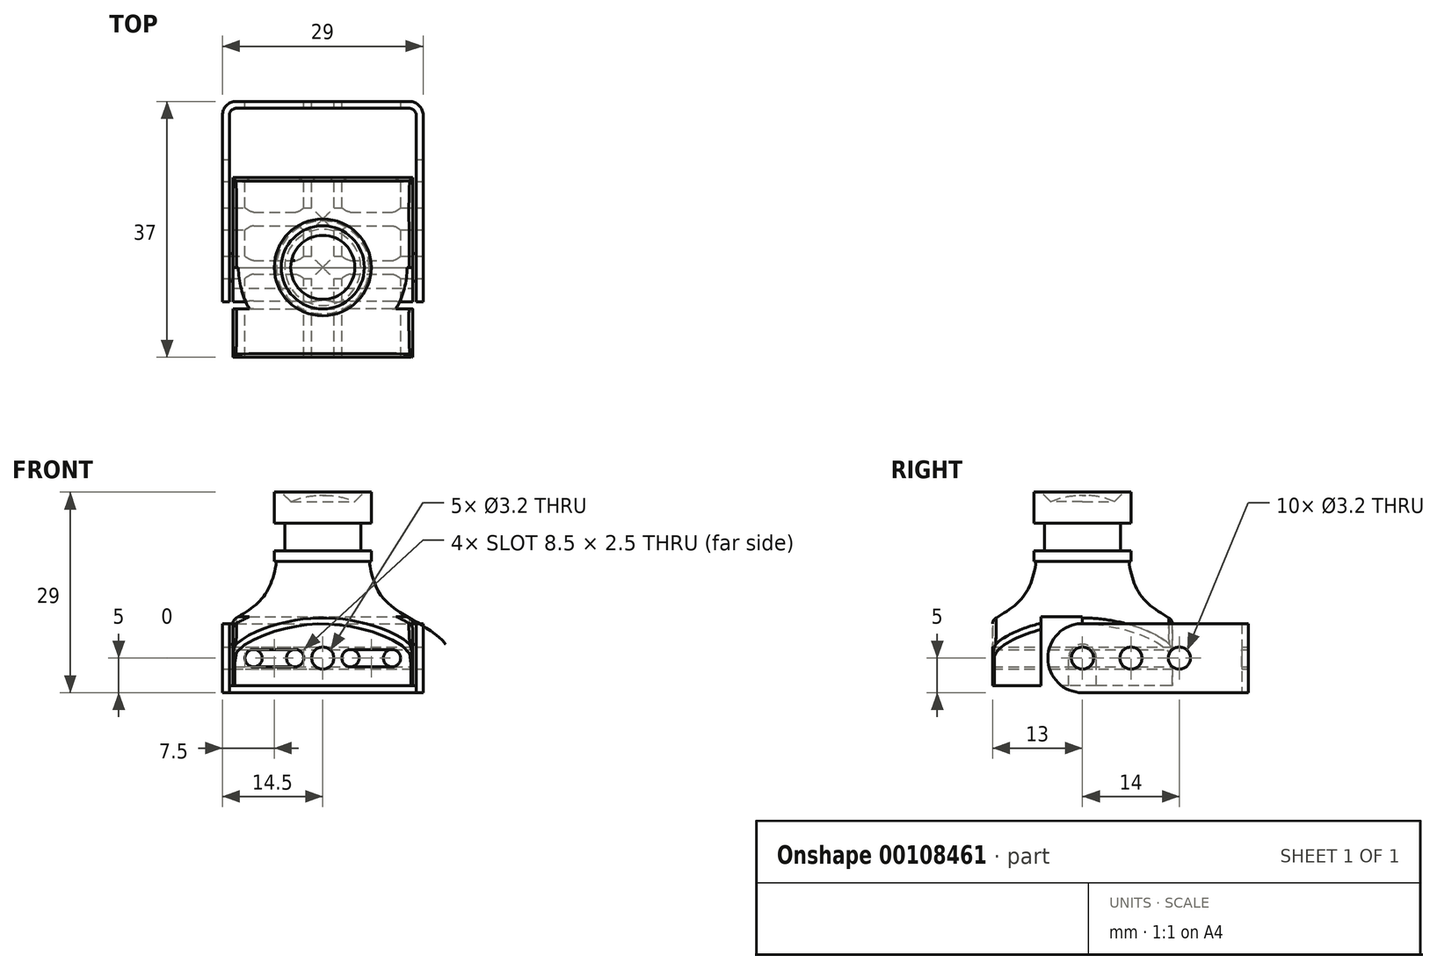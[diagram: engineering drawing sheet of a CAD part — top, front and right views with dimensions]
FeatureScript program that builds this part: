
annotation { "Feature Type Name" : "Feature", "Feature Type Description" : "" }
export const myFeature = defineFeature(function(context is Context, id is Id, definition is map)
    precondition{}
    {
        {
            var Q0;
            Q0=qCreatedBy(makeId("Front.planeOp"),FACE);
            var sketch = newSketch(context, id + "F0", { "sketchPlane" : qUnion([Q0])});
            skLineSegment(sketch, "E0", {"start": v(0, 0) * mm, "end": v(0, 27.5) * mm});
            skLineSegment(sketch, "E1", {"start": v(7, 28) * mm, "end": v(7, 23.5) * mm});
            skLineSegment(sketch, "E2", {"start": v(7, 23.5) * mm, "end": v(5.5, 23.5) * mm});
            skLineSegment(sketch, "E3", {"start": v(5.5, 23.5) * mm, "end": v(5.5, 19.5) * mm});
            skLineSegment(sketch, "E4", {"start": v(5.5, 19.5) * mm, "end": v(7, 19.5) * mm});
            skLineSegment(sketch, "E5", {"start": v(7, 19.5) * mm, "end": v(7, 18) * mm});
            skLineSegment(sketch, "E6", {"start": v(7, 18) * mm, "end": v(6.7, 18) * mm});
            skFitSpline(sketch, "E7", {"points": [v(6.7, 18) * mm, v(8.96, 12.41) * mm, v(13.5, 9.25) * mm, v(17.33, 6.49) * mm, v(18.5, 4) * mm], "startDerivative": vector(3.38, -24.57) * mm, "endDerivative": vector(0, -14.16) * mm});
            skLineSegment(sketch, "E8", {"start": v(7, 28) * mm, "end": v(6, 28) * mm});
            skLineSegment(sketch, "E9", {"start": v(6, 28) * mm, "end": v(4.63, 26.63) * mm});
            skFitSpline(sketch, "E10", {"points": [v(0, 27.5) * mm, v(4.63, 26.63) * mm], "startDerivative": vector(5.21, 0.16) * mm, "endDerivative": vector(4.71, -2.1) * mm});
            skLineSegment(sketch, "E11", {"start": v(18.5, 4) * mm, "end": v(18.5, 0) * mm});
            skLineSegment(sketch, "E12", {"start": v(18.5, 0) * mm, "end": v(0, 0) * mm});
            skSolve(sketch);
        }
        {
            var Q0;
            Q0 = qSketchRegion(id + "F0", true);
            var Q1;
            Q1=sQuery(id+"F0.wireOp",EDGE,"E0");
            revolve(context, id + "F1", {"entities" : qUnion([Q0]), "axis" : qUnion([Q1]), "revolveType" : RevolveType.FULL});
        }
        {
            var Q0;
            Q0=qCreatedBy(makeId("Right.planeOp"),FACE);
            var sketch = newSketch(context, id + "F2", { "sketchPlane" : qUnion([Q0])});
            skLineSegment(sketch, "E13", {"start": v(-13, 0) * mm, "end": v(-13, 12) * mm});
            skLineSegment(sketch, "E14", {"start": v(-13, 12) * mm, "end": v(-20, 12) * mm});
            skLineSegment(sketch, "E15", {"start": v(-20, 12) * mm, "end": v(-20, -2) * mm});
            skLineSegment(sketch, "E16", {"start": v(-20, -2) * mm, "end": v(0, -2) * mm});
            skLineSegment(sketch, "E17", {"start": v(-13, 0) * mm, "end": v(0, 0) * mm});
            skLineSegment(sketch, "E18.MirrorCS", {"start": v(13, 0) * mm, "end": v(13, 12) * mm});
            skLineSegment(sketch, "E19.MirrorCS", {"start": v(20, 12) * mm, "end": v(20, -2) * mm});
            skLineSegment(sketch, "E20.MirrorCS", {"start": v(13, 0) * mm, "end": v(0, 0) * mm});
            skLineSegment(sketch, "E21.MirrorCS", {"start": v(20, -2) * mm, "end": v(0, -2) * mm});
            skLineSegment(sketch, "E22.MirrorCS", {"start": v(13, 12) * mm, "end": v(20, 12) * mm});
            skSolve(sketch);
        }
        {
            var Q0;
            Q0 = qSketchRegion(id + "F2", true);
            extrude(context, id + "F3", {"entities" : qUnion([Q0]), "operationType" : NewBodyOperationType.REMOVE, "endBound" : BoundingType.THROUGH_ALL, "oppositeDirection" : true, "depth" : 25 * mm, "hasSecondDirection" : true, "secondDirectionBound" : SecondDirectionBoundingType.THROUGH_ALL, "secondDirectionOppositeDirection" : false, "secondDirectionDepth" : 25 * mm});
        }
        {
            var Q0;
            Q0=qCreatedBy(makeId("Front.planeOp"),FACE);
            var sketch = newSketch(context, id + "F4", { "sketchPlane" : qUnion([Q0])});
            skLineSegment(sketch, "E23", {"start": v(-13, 0) * mm, "end": v(-13, 12) * mm});
            skLineSegment(sketch, "E24", {"start": v(-13, 12) * mm, "end": v(-20, 12) * mm});
            skLineSegment(sketch, "E25", {"start": v(-20, 12) * mm, "end": v(-20, -2) * mm});
            skLineSegment(sketch, "E26", {"start": v(-20, -2) * mm, "end": v(0, -2) * mm});
            skLineSegment(sketch, "E27", {"start": v(-13, 0) * mm, "end": v(0, 0) * mm});
            skLineSegment(sketch, "E28.MirrorCS", {"start": v(13, 0) * mm, "end": v(13, 12) * mm});
            skLineSegment(sketch, "E29.MirrorCS", {"start": v(13, 12) * mm, "end": v(20, 12) * mm});
            skLineSegment(sketch, "E30.MirrorCS", {"start": v(20, -2) * mm, "end": v(0, -2) * mm});
            skLineSegment(sketch, "E31.MirrorCS", {"start": v(20, 12) * mm, "end": v(20, -2) * mm});
            skLineSegment(sketch, "E32.MirrorCS", {"start": v(13, 0) * mm, "end": v(0, 0) * mm});
            skSolve(sketch);
        }
        {
            var Q0;
            Q0 = qSketchRegion(id + "F4", true);
            extrude(context, id + "F5", {"entities" : qUnion([Q0]), "operationType" : NewBodyOperationType.REMOVE, "endBound" : BoundingType.THROUGH_ALL, "oppositeDirection" : true, "depth" : 25 * mm, "hasSecondDirection" : true, "secondDirectionBound" : SecondDirectionBoundingType.THROUGH_ALL, "secondDirectionOppositeDirection" : false, "secondDirectionDepth" : 25 * mm});
        }
        {
            var Q0;
            Q0=makeQuery(id+"F3.boolean.opBoolean","INTERSECT",EDGE,{"derivedFrom":[makeQuery(id+"F1.opRevolve","SWEPT_FACE",FACE,{"disambiguationData":[OSD([sQuery(id+"F0.wireOp",EDGE,"E7")])]}),makeQuery(id+"F3.opExtrude","SWEPT_FACE",FACE,{"disambiguationData":[OSD([sQuery(id+"F2.wireOp",EDGE,"E13")])]})]});
            var Q1;
            Q1=makeQuery(id+"F5.boolean.opBoolean","INTERSECT",EDGE,{"derivedFrom":[makeQuery(id+"F1.opRevolve","SWEPT_FACE",FACE,{"disambiguationData":[OSD([sQuery(id+"F0.wireOp",EDGE,"E7")])]}),makeQuery(id+"F5.opExtrude","SWEPT_FACE",FACE,{"disambiguationData":[OSD([sQuery(id+"F4.wireOp",EDGE,"E23")])]})]});
            var Q2;
            Q2=makeQuery(id+"F3.boolean.opBoolean","INTERSECT",EDGE,{"derivedFrom":[makeQuery(id+"F1.opRevolve","SWEPT_FACE",FACE,{"disambiguationData":[OSD([sQuery(id+"F0.wireOp",EDGE,"E7")])]}),makeQuery(id+"F3.opExtrude","SWEPT_FACE",FACE,{"disambiguationData":[OSD([sQuery(id+"F2.wireOp",EDGE,"E18.MirrorCS")])]})]});
            var Q3;
            Q3=makeQuery(id+"F5.boolean.opBoolean","INTERSECT",EDGE,{"derivedFrom":[makeQuery(id+"F1.opRevolve","SWEPT_FACE",FACE,{"disambiguationData":[OSD([sQuery(id+"F0.wireOp",EDGE,"E7")])]}),makeQuery(id+"F5.opExtrude","SWEPT_FACE",FACE,{"disambiguationData":[OSD([sQuery(id+"F4.wireOp",EDGE,"E28.MirrorCS")])]})]});
            fillet(context, id + "F6", {"entities" : qUnion([Q0, Q1, Q2, Q3]), "radius" : 1 * mm, "tangentPropagation" : true, "allowEdgeOverflow" : false});
        }
        {
            var Q0;
            Q0=makeQuery(id+"F5.boolean.opBoolean","COPY",FACE,{"derivedFrom":makeQuery(id+"F5.opExtrude","SWEPT_FACE",FACE,{"disambiguationData":[OSD([sQuery(id+"F4.wireOp",EDGE,"E28.MirrorCS")])]})});
            var sketch = newSketch(context, id + "F7", { "sketchPlane" : qUnion([Q0])});
            skLineSegment(sketch, "E33.bottom", {"start": v(-2, 0) * mm, "end": v(2, 0) * mm});
            skLineSegment(sketch, "E33.left", {"start": v(-2, 0) * mm, "end": v(-2, 4) * mm});
            skLineSegment(sketch, "E33.right", {"start": v(2, 0) * mm, "end": v(2, 4) * mm});
            skPoint(sketch, "E34", {"position": v(0, 0) * mm});
            skArc(sketch, "E35", {"start": v(2, 4) * mm, "mid": v(0, 6) * mm, "end": v(-2, 4) * mm});
            skSolve(sketch);
        }
        {
            var Q0;
            Q0 = qSketchRegion(id + "F7", true);
            extrude(context, id + "F8", {"entities" : qUnion([Q0]), "operationType" : NewBodyOperationType.ADD, "depth" : .5 * mm});
        }
        {
            var Q0;
            Q0=makeQuery(id+"F5.boolean.opBoolean","COPY",FACE,{"derivedFrom":makeQuery(id+"F5.opExtrude","SWEPT_FACE",FACE,{"disambiguationData":[OSD([sQuery(id+"F4.wireOp",EDGE,"E23")])]})});
            var sketch = newSketch(context, id + "F9", { "sketchPlane" : qUnion([Q0])});
            skLineSegment(sketch, "E36.0", {"start": v(-2, 0) * mm, "end": v(-2, 4) * mm});
            skArc(sketch, "E37.0", {"start": v(-2, 4) * mm, "mid": v(0, 6) * mm, "end": v(2, 4) * mm});
            skLineSegment(sketch, "E38.0", {"start": v(2, 0) * mm, "end": v(2, 4) * mm});
            skLineSegment(sketch, "E39.0", {"start": v(2, 0) * mm, "end": v(-2, 0) * mm});
            skSolve(sketch);
        }
        {
            var Q0;
            Q0 = qSketchRegion(id + "F9", true);
            extrude(context, id + "F10", {"entities" : qUnion([Q0]), "operationType" : NewBodyOperationType.ADD, "depth" : .5 * mm});
        }
        {
            var Q0;
            Q0=makeQuery(id+"F8.opExtrude","CAP_FACE",FACE,{"disambiguationData":[OSD([sQuery(id+"F7.wireOp",EDGE,"E33.bottom"),sQuery(id+"F7.wireOp",EDGE,"E33.left"),sQuery(id+"F7.wireOp",EDGE,"E33.right"),sQuery(id+"F7.wireOp",EDGE,"E35")])],"isStart":false});
            var sketch = newSketch(context, id + "F11", { "sketchPlane" : qUnion([Q0])});
            skCircle(sketch, "E40", {"center": v(0, 4) * mm, "radius": 1.5 * mm});
            skSolve(sketch);
        }
        {
            var Q0;
            Q0 = qSketchRegion(id + "F11", true);
            extrude(context, id + "F12", {"entities" : qUnion([Q0]), "operationType" : NewBodyOperationType.ADD, "depth" : 1 * mm});
        }
        {
            var Q0;
            Q0=makeQuery(id+"F10.opExtrude","CAP_FACE",FACE,{"disambiguationData":[OSD([sQuery(id+"F9.wireOp",EDGE,"E36.0"),sQuery(id+"F9.wireOp",EDGE,"E37.0"),sQuery(id+"F9.wireOp",EDGE,"E38.0"),sQuery(id+"F9.wireOp",EDGE,"E39.0")])],"isStart":false});
            var sketch = newSketch(context, id + "F13", { "sketchPlane" : qUnion([Q0])});
            skCircle(sketch, "E41", {"center": v(0, 4) * mm, "radius": 1.5 * mm});
            skSolve(sketch);
        }
        {
            var Q0;
            Q0 = qSketchRegion(id + "F13", true);
            extrude(context, id + "F14", {"entities" : qUnion([Q0]), "operationType" : NewBodyOperationType.ADD, "depth" : 1 * mm});
        }
        {
            var Q0;
            Q0=makeQuery(id+"F12.opExtrude","CAP_FACE",FACE,{"disambiguationData":[OSD([sQuery(id+"F11.wireOp",EDGE,"E40")])],"isStart":false});
            var sketch = newSketch(context, id + "F15", { "sketchPlane" : qUnion([Q0])});
            skPoint(sketch, "E42", {"position": v(0, 4) * mm});
            skSolve(sketch);
        }
        {
            var Q0;
            Q0=sQuery(id+"F15.wireOp",VERTEX,"E42");
            var Q1;
            Q1=makeQuery(id+"F1.opRevolve","SWEPT_BODY",BODY,{"disambiguationData":[OSD([sQuery(id+"F0.wireOp",EDGE,"E0"),sQuery(id+"F0.wireOp",EDGE,"E1"),sQuery(id+"F0.wireOp",EDGE,"E2"),sQuery(id+"F0.wireOp",EDGE,"E3"),sQuery(id+"F0.wireOp",EDGE,"E4"),sQuery(id+"F0.wireOp",EDGE,"E5"),sQuery(id+"F0.wireOp",EDGE,"E6"),sQuery(id+"F0.wireOp",EDGE,"E7"),sQuery(id+"F0.wireOp",EDGE,"E8"),sQuery(id+"F0.wireOp",EDGE,"E9"),sQuery(id+"F0.wireOp",EDGE,"E10"),sQuery(id+"F0.wireOp",EDGE,"E11"),sQuery(id+"F0.wireOp",EDGE,"E12")])]});
            hole(context, id + "F16", {"style" : HoleStyle.SIMPLE, "endStyle" : HoleEndStyle.BLIND, "standardTappedOrClearance" : lookupTablePath({ "standard" : "ANSI", "engagement" : "75%", "pitch" : "40 tpi", "size" : "#4", "type" : "Tapped" }), "standardBlindInLast" : lookupTablePath({ "standard" : "ANSI", "engagement" : "75%", "pitch" : "40 tpi", "size" : "#4", "type" : "Tapped" }), "holeDiameter" : 2.26 * mm, "holeDepth" : 5 * mm, "startFromSketch" : true, "locations" : qUnion([Q0]), "scope" : qUnion([Q1]), "majorDiameter" : 2.84 * mm});
        }
        {
            var Q0;
            Q0=makeQuery(id+"F14.opExtrude","CAP_FACE",FACE,{"disambiguationData":[OSD([sQuery(id+"F13.wireOp",EDGE,"E41")])],"isStart":false});
            var sketch = newSketch(context, id + "F17", { "sketchPlane" : qUnion([Q0])});
            skPoint(sketch, "E43", {"position": v(0, 4) * mm});
            skSolve(sketch);
        }
        {
            var Q0;
            Q0=sQuery(id+"F17.wireOp",VERTEX,"E43");
            var Q1;
            Q1=makeQuery(id+"F1.opRevolve","SWEPT_BODY",BODY,{"disambiguationData":[OSD([sQuery(id+"F0.wireOp",EDGE,"E0"),sQuery(id+"F0.wireOp",EDGE,"E1"),sQuery(id+"F0.wireOp",EDGE,"E2"),sQuery(id+"F0.wireOp",EDGE,"E3"),sQuery(id+"F0.wireOp",EDGE,"E4"),sQuery(id+"F0.wireOp",EDGE,"E5"),sQuery(id+"F0.wireOp",EDGE,"E6"),sQuery(id+"F0.wireOp",EDGE,"E7"),sQuery(id+"F0.wireOp",EDGE,"E8"),sQuery(id+"F0.wireOp",EDGE,"E9"),sQuery(id+"F0.wireOp",EDGE,"E10"),sQuery(id+"F0.wireOp",EDGE,"E11"),sQuery(id+"F0.wireOp",EDGE,"E12")])]});
            hole(context, id + "F18", {"style" : HoleStyle.SIMPLE, "endStyle" : HoleEndStyle.BLIND, "standardTappedOrClearance" : lookupTablePath({ "standard" : "ANSI", "engagement" : "75%", "pitch" : "40 tpi", "size" : "#4", "type" : "Tapped" }), "standardBlindInLast" : lookupTablePath({ "standard" : "ANSI", "engagement" : "75%", "pitch" : "40 tpi", "size" : "#4", "type" : "Tapped" }), "holeDiameter" : 2.26 * mm, "holeDepth" : 5 * mm, "startFromSketch" : true, "locations" : qUnion([Q0]), "scope" : qUnion([Q1]), "majorDiameter" : 2.84 * mm});
        }
        {
            var Q0;
            Q0=qCreatedBy(makeId("Top.planeOp"),FACE);
            cPlane(context, id + "F19", {"entities" : qUnion([Q0]), "cplaneType" : CPlaneType.OFFSET, "offset" : 4 * mm, "width" : 150 * mm, "height" : 150 * mm});
        }
        {
            var Q0;
            Q0=qCreatedBy(id+"F19.planeOp",FACE);
            var sketch = newSketch(context, id + "F20", { "sketchPlane" : qUnion([Q0])});
            skLineSegment(sketch, "E44", {"start": v(-13.5, -5) * mm, "end": v(-13.5, 22) * mm});
            skLineSegment(sketch, "E45", {"start": v(-12.5, 23) * mm, "end": v(0, 23) * mm});
            skLineSegment(sketch, "E46.0", {"start": v(-12.5, 24) * mm, "end": v(0, 24) * mm});
            skLineSegment(sketch, "E46.1", {"start": v(-14.5, -5) * mm, "end": v(-14.5, 22) * mm});
            skLineSegment(sketch, "E47", {"start": v(-14.5, -5) * mm, "end": v(-13.5, -5) * mm});
            skPoint(sketch, "E48.visualSharp", {"position": v(-13.5, 23) * mm});
            skArc(sketch, "E48.filletArc", {"start": v(-12.5, 23) * mm, "mid": v(-13.2, 22.7) * mm, "end": v(-13.5, 22) * mm});
            skPoint(sketch, "E49.visualSharp", {"position": v(-14.5, 24) * mm});
            skArc(sketch, "E49.filletArc", {"start": v(-12.5, 24) * mm, "mid": v(-13.91, 23.41) * mm, "end": v(-14.5, 22) * mm});
            skLineSegment(sketch, "E50.MirrorCS", {"start": v(14.5, -5) * mm, "end": v(13.5, -5) * mm});
            skArc(sketch, "E51.MirrorCS", {"start": v(12.5, 23) * mm, "mid": v(13.2, 22.7) * mm, "end": v(13.5, 22) * mm});
            skArc(sketch, "E52.MirrorCS", {"start": v(12.5, 24) * mm, "mid": v(13.91, 23.41) * mm, "end": v(14.5, 22) * mm});
            skLineSegment(sketch, "E53.MirrorCS", {"start": v(14.5, -5) * mm, "end": v(14.5, 22) * mm});
            skPoint(sketch, "E54.MirrorP", {"position": v(14.5, 24) * mm});
            skLineSegment(sketch, "E55.MirrorCS", {"start": v(12.5, 23) * mm, "end": v(0, 23) * mm});
            skPoint(sketch, "E56.MirrorP", {"position": v(13.5, 23) * mm});
            skLineSegment(sketch, "E57.MirrorCS", {"start": v(13.5, -5) * mm, "end": v(13.5, 22) * mm});
            skLineSegment(sketch, "E58.MirrorCS", {"start": v(12.5, 24) * mm, "end": v(0, 24) * mm});
            skSolve(sketch);
        }
        {
            var Q0;
            Q0 = qSketchRegion(id + "F20", true);
            extrude(context, id + "F21", {"entities" : qUnion([Q0]), "endBound" : BoundingType.SYMMETRIC, "depth" : 10 * mm});
        }
        {
            var Q0;
            Q0=makeQuery(id+"F21.opExtrude","SWEPT_FACE",FACE,{"disambiguationData":[OSD([sQuery(id+"F20.wireOp",EDGE,"E53.MirrorCS")])]});
            var sketch = newSketch(context, id + "F22", { "sketchPlane" : qUnion([Q0])});
            skArc(sketch, "E59", {"start": v(0, 9) * mm, "mid": v(-5, 4) * mm, "end": v(0, -1) * mm});
            skLineSegment(sketch, "E60", {"start": v(0, -1) * mm, "end": v(0, -2) * mm});
            skLineSegment(sketch, "E61", {"start": v(0, -2) * mm, "end": v(-6, -2) * mm});
            skLineSegment(sketch, "E62", {"start": v(-6, -2) * mm, "end": v(-6, 10) * mm});
            skLineSegment(sketch, "E63", {"start": v(-6, 10) * mm, "end": v(0, 10) * mm});
            skLineSegment(sketch, "E64", {"start": v(0, 10) * mm, "end": v(0, 9) * mm});
            skSolve(sketch);
        }
        {
            var Q0;
            Q0 = qSketchRegion(id + "F22", true);
            extrude(context, id + "F23", {"entities" : qUnion([Q0]), "operationType" : NewBodyOperationType.REMOVE, "endBound" : BoundingType.THROUGH_ALL, "oppositeDirection" : true, "depth" : 25 * mm});
        }
        {
            var Q0;
            Q0=makeQuery(id+"F21.opExtrude","SWEPT_FACE",FACE,{"disambiguationData":[OSD([sQuery(id+"F20.wireOp",EDGE,"E53.MirrorCS")])]});
            var sketch = newSketch(context, id + "F24", { "sketchPlane" : qUnion([Q0])});
            skLineSegment(sketch, "E65", {"start": v(0, 4) * mm, "end": v(21.45, 4) * mm, "construction": true});
            skCircle(sketch, "E66", {"center": v(0, 4) * mm, "radius": 1.6 * mm});
            skCircle(sketch, "E67", {"center": v(7, 4) * mm, "radius": 1.6 * mm});
            skCircle(sketch, "E68", {"center": v(14, 4) * mm, "radius": 1.6 * mm});
            skSolve(sketch);
        }
        {
            var Q0;
            Q0 = qSketchRegion(id + "F24", true);
            extrude(context, id + "F25", {"entities" : qUnion([Q0]), "operationType" : NewBodyOperationType.REMOVE, "endBound" : BoundingType.THROUGH_ALL, "oppositeDirection" : true, "depth" : 25 * mm});
        }
        {
            var Q0;
            Q0=makeQuery(id+"F21.opExtrude","SWEPT_FACE",FACE,{"disambiguationData":[OSD([sQuery(id+"F20.wireOp",EDGE,"E46.0"),sQuery(id+"F20.wireOp",EDGE,"E58.MirrorCS")])]});
            var sketch = newSketch(context, id + "F26", { "sketchPlane" : qUnion([Q0])});
            skCircle(sketch, "E69", {"center": v(0, 4) * mm, "radius": 1.6 * mm});
            skArc(sketch, "E70", {"start": v(10, 2.75) * mm, "mid": v(11.25, 4) * mm, "end": v(10, 5.25) * mm});
            skArc(sketch, "E71", {"start": v(4, 5.25) * mm, "mid": v(2.75, 4) * mm, "end": v(4, 2.75) * mm});
            skLineSegment(sketch, "E72", {"start": v(10, 2.75) * mm, "end": v(4, 2.75) * mm});
            skLineSegment(sketch, "E73", {"start": v(10, 5.25) * mm, "end": v(4, 5.25) * mm});
            skArc(sketch, "E74.MirrorCS", {"start": v(-10, 2.75) * mm, "mid": v(-11.25, 4) * mm, "end": v(-10, 5.25) * mm});
            skLineSegment(sketch, "E75.MirrorCS", {"start": v(-10, 2.75) * mm, "end": v(-4, 2.75) * mm});
            skLineSegment(sketch, "E76.MirrorCS", {"start": v(-10, 5.25) * mm, "end": v(-4, 5.25) * mm});
            skArc(sketch, "E77.MirrorCS", {"start": v(-4, 5.25) * mm, "mid": v(-2.75, 4) * mm, "end": v(-4, 2.75) * mm});
            skSolve(sketch);
        }
        {
            var Q0;
            Q0 = qSketchRegion(id + "F26", true);
            extrude(context, id + "F27", {"entities" : qUnion([Q0]), "operationType" : NewBodyOperationType.REMOVE, "endBound" : BoundingType.THROUGH_ALL, "oppositeDirection" : true, "depth" : 25 * mm});
        }
    });
